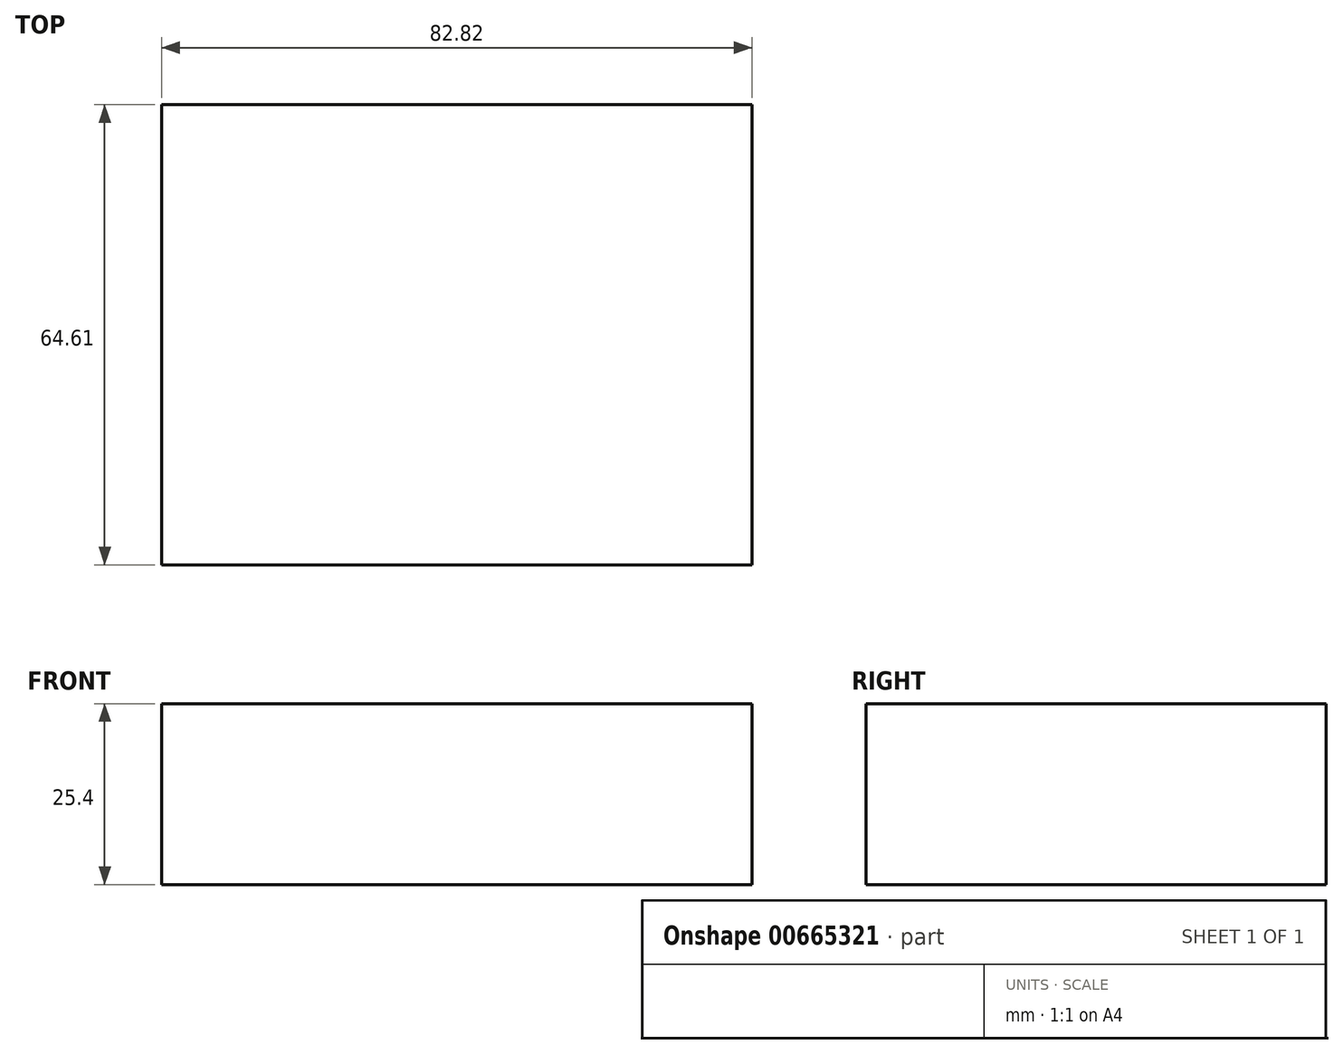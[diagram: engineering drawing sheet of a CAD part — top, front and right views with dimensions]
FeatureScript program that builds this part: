
annotation { "Feature Type Name" : "Feature", "Feature Type Description" : "" }
export const myFeature = defineFeature(function(context is Context, id is Id, definition is map)
    precondition{}
    {
        {
            var Q0;
            Q0=qCreatedBy(makeId("Top.planeOp"),FACE);
            var sketch = newSketch(context, id + "F0", { "sketchPlane" : qUnion([Q0])});
            skLineSegment(sketch, "E0.bottom", {"start": v(-39.92, 29.49) * mm, "end": v(42.9, 29.49) * mm});
            skLineSegment(sketch, "E0.top", {"start": v(-39.92, -35.12) * mm, "end": v(42.9, -35.12) * mm});
            skLineSegment(sketch, "E0.left", {"start": v(-39.92, 29.49) * mm, "end": v(-39.92, -35.12) * mm});
            skLineSegment(sketch, "E0.right", {"start": v(42.9, 29.49) * mm, "end": v(42.9, -35.12) * mm});
            skSolve(sketch);
        }
        {
            var Q0;
            Q0 = qSketchRegion(id + "F0", true);
            extrude(context, id + "F1", {"entities" : qUnion([Q0]), "depth" : 25.4 * mm, "offsetDistance" : 25.4 * mm});
        }
    });
